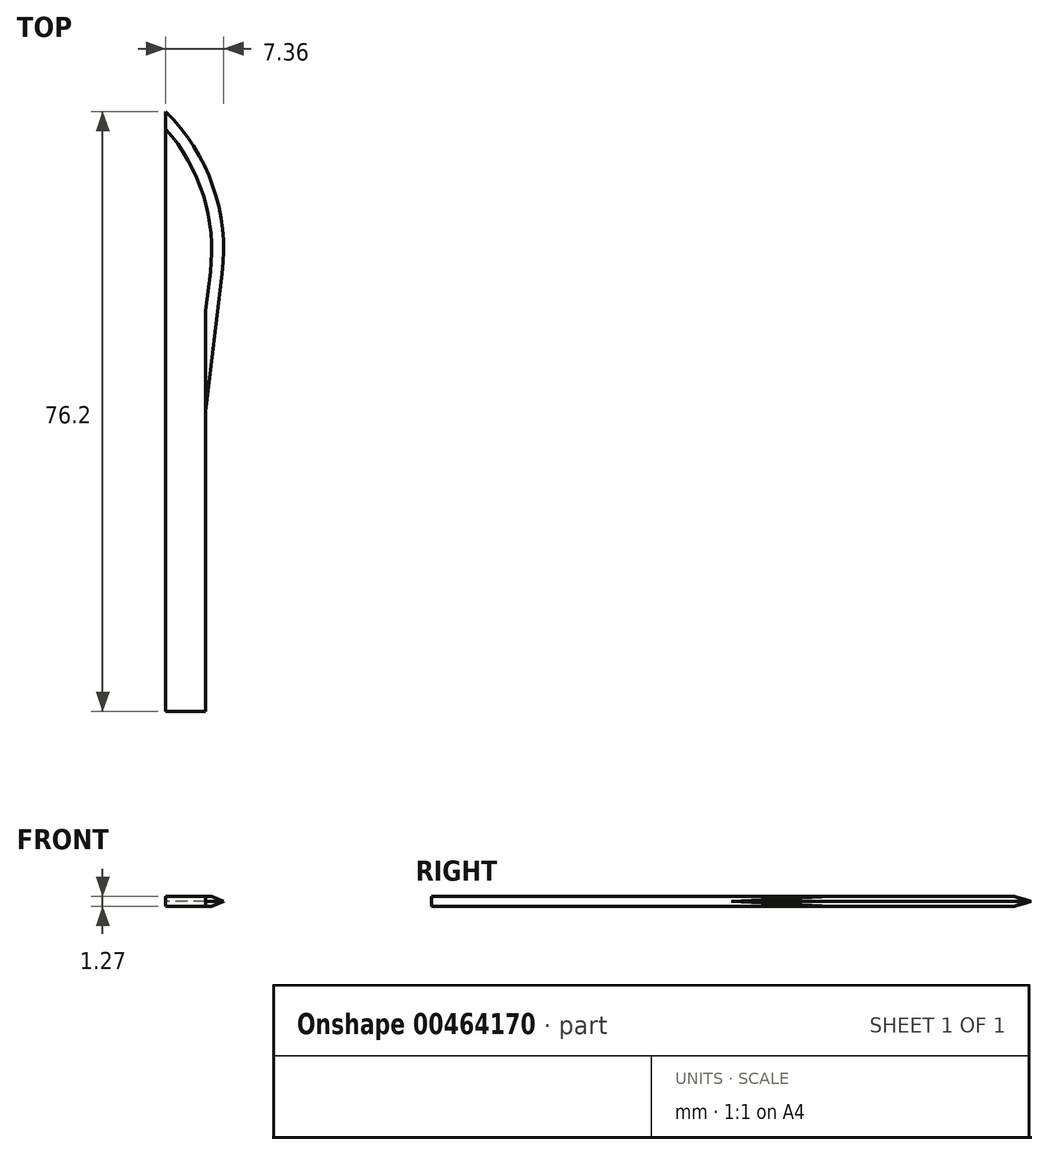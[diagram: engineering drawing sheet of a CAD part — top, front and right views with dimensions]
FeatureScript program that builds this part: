
annotation { "Feature Type Name" : "Feature", "Feature Type Description" : "" }
export const myFeature = defineFeature(function(context is Context, id is Id, definition is map)
    precondition{}
    {
        {
            var Q0;
            Q0=qCreatedBy(makeId("Top.planeOp"),FACE);
            var sketch = newSketch(context, id + "F0", { "sketchPlane" : qUnion([Q0])});
            skLineSegment(sketch, "E0", {"start": v(-36.83, 0) * mm, "end": v(-31.75, 0) * mm});
            skLineSegment(sketch, "E1", {"start": v(-36.83, 0) * mm, "end": v(-36.83, 25.4) * mm});
            skLineSegment(sketch, "E2", {"start": v(-31.75, 0) * mm, "end": v(-31.75, 25.4) * mm});
            skLineSegment(sketch, "E3", {"start": v(-31.75, 25.4) * mm, "end": v(-31.75, 38.1) * mm});
            skLineSegment(sketch, "E4", {"start": v(-36.83, 25.4) * mm, "end": v(-36.83, 76.2) * mm});
            skLineSegment(sketch, "E5", {"start": v(-31.75, 38.1) * mm, "end": v(-29.65, 55.64) * mm});
            skArc(sketch, "E6", {"start": v(-29.65, 55.64) * mm, "mid": v(-30.86, 66.75) * mm, "end": v(-36.83, 76.2) * mm});
            skSolve(sketch);
        }
        {
            var Q0;
            Q0=makeQuery(id+"F0.imprint","IMPRINT",FACE,{"disambiguationData":[TD([[makeQuery(id+"F0.imprint","IMPRINT",EDGE,{"derivedFrom":sQuery(id+"F0.wireOp",EDGE,"E0")}),1.0]])]});
            extrude(context, id + "F1", {"entities" : qUnion([Q0]), "depth" : 1.27 * mm});
        }
        {
            var Q0;
            Q0=makeQuery(id+"F1.opExtrude","CAP_EDGE",EDGE,{"disambiguationData":[OSD([sQuery(id+"F0.wireOp",EDGE,"E6")])],"isStart":true});
            chamfer(context, id + "F2", {"entities" : qUnion([Q0]), "chamferType" : ChamferType.TWO_OFFSETS, "width1" : 0.64 * mm, "oppositeDirection" : false, "width2" : 1.52 * mm, "tangentPropagation" : true});
        }
        {
            var Q0;
            Q0=makeQuery(id+"F1.opExtrude","CAP_EDGE",EDGE,{"disambiguationData":[OSD([sQuery(id+"F0.wireOp",EDGE,"E6")])],"isStart":false});
            chamfer(context, id + "F3", {"entities" : qUnion([Q0]), "chamferType" : ChamferType.TWO_OFFSETS, "width1" : 1.52 * mm, "oppositeDirection" : false, "width2" : 0.64 * mm, "tangentPropagation" : true});
        }
    });
